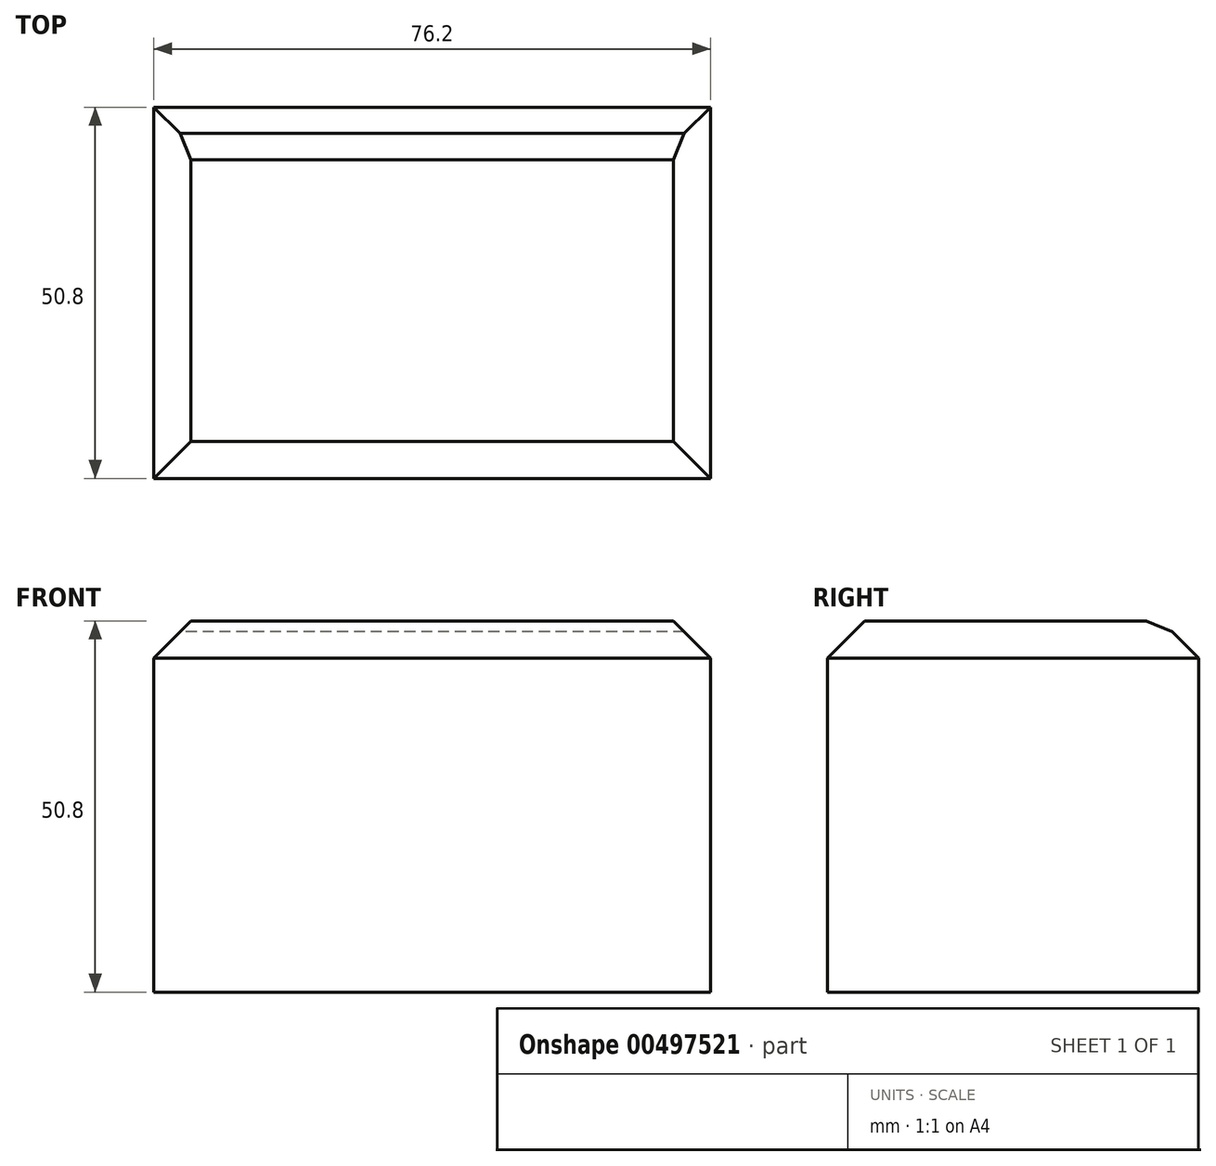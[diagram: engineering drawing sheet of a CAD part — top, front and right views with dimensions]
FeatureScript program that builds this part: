
annotation { "Feature Type Name" : "Feature", "Feature Type Description" : "" }
export const myFeature = defineFeature(function(context is Context, id is Id, definition is map)
    precondition{}
    {
        {
            var Q0;
            Q0=qCreatedBy(makeId("Top.planeOp"),FACE);
            var sketch = newSketch(context, id + "F0", { "sketchPlane" : qUnion([Q0])});
            skLineSegment(sketch, "E0.bottom", {"start": v(-18.9, 30.7) * mm, "end": v(57.3, 30.7) * mm});
            skLineSegment(sketch, "E0.top", {"start": v(-18.9, -20.1) * mm, "end": v(57.3, -20.1) * mm});
            skLineSegment(sketch, "E0.left", {"start": v(-18.9, 30.7) * mm, "end": v(-18.9, -20.1) * mm});
            skLineSegment(sketch, "E0.right", {"start": v(57.3, 30.7) * mm, "end": v(57.3, -20.1) * mm});
            skSolve(sketch);
        }
        {
            var Q0;
            Q0 = qSketchRegion(id + "F0", true);
            extrude(context, id + "F1", {"entities" : qUnion([Q0]), "depth" : 50.8 * mm});
        }
        {
            var Q0;
            Q0=makeQuery(id+"F1.opExtrude","CAP_EDGE",EDGE,{"disambiguationData":[OSD([sQuery(id+"F0.wireOp",EDGE,"E0.bottom")])],"isStart":false});
            chamfer(context, id + "F2", {"entities" : qUnion([Q0]), "width" : 5.08 * mm, "tangentPropagation" : true});
        }
        {
            var Q0;
            Q0=makeQuery(id+"F1.opExtrude","CAP_FACE",FACE,{"disambiguationData":[OSD([sQuery(id+"F0.wireOp",EDGE,"E0.bottom"),sQuery(id+"F0.wireOp",EDGE,"E0.top"),sQuery(id+"F0.wireOp",EDGE,"E0.left"),sQuery(id+"F0.wireOp",EDGE,"E0.right")])],"isStart":false});
            chamfer(context, id + "F3", {"entities" : qUnion([Q0]), "width" : 5.08 * mm, "tangentPropagation" : true});
        }
    });
